# Revit family: 2019_ES_Ventana_Anicolor_Aji-HO-CE_2-Hojas_Oscilobatiente
name_source: partatom
category: Windows
units: mm (PartAtom-declared; Revit-internal decimal feet)

## family parameters
Always vertical = Yes
Cut with Voids When Loaded = No
Host = Wall
OmniClass Number = 23.30.20.00
OmniClass Title = Windows
Room Calculation Point = No
Shared = No

## types (2) — shared parameters
Abatible = No
Altura Máxima = 0.000 mm
Altura Mínima = 0.000 mm
Altura de antepecho por defecto = 500.000 mm
Altura mínima necessária = 0.000 mm
Analytic Construction = 1/4 in Pilkington single glazing
AnchoMarcoCentral = 101.000 mm
AnchoMarcoPerimetral = 69.300 mm
Anchura Máxima = 0.000 mm
Anchura Mínima = 0.000 mm
Aro = Aluminio
BIM Support = https://bimsupport.info
BIMEelementExpiryDate = 10/01/2021
BIMElementIssueDate = 10/01/2020
Bimetica = http://www.bimetica.com
BimeticaProductProfileURL = https://bimetica.com
ConfiguraçãoPoliamida = 273800 - 241200 - 961859
ControloDeFumos = No
CustoEnergéticoMj = 0 J
Define Thermal Properties by = Schematic Type
Description = Ventana 2 Hojas Practicables AJi HO CE de Anicolor
Enchimento = Vidro
Espaço livre acesso = 0.000 mm
EspesorPerfilesAluminio = 0.000 mm
EspessuraMaximaDoVidro = 0.000 mm
EspessuraMinimaDoVidro = 0.000 mm
Espuma = Espuma PIR entre varillas, galce del vidrio y marco
EstanquidadeÀÁgua = Clase E1650
GarantiaEstendida = Yes
GrosorHoja = 70.300 mm
Heat Transfer Coefficient (U) = 6.7018 W/(m²·K)
Historial = (RVT2019-V01) Creación de elemento.
HousingMaterial = <By Category>
IFCClassificação = IfcWindow
IfcExportAs = IfcWindow
IfcExportType = DoublePanelVertical
Intercalar = Technoform Warm Edge
IsExternal = Yes
LarguraPoliamidaAroFixo = 30.000 mm
LarguraPoliamidaFolha = 16.000 mm
Length = 0.000 mm
LicenseNumber = XXX-XXXX4564
Manija = Yes
Manufacturer = Anicolor
Marcado CE = Yes
MasterformatCode = 08 50 00
MasterformatTitle = Windows
Model = Aji HO CE
Motorizada = No
NúmeroSérie = AJi HO CE
OmniclassCode = 23-17 13 00
OmniclassTitle = Windows
Operation = Practicable. Ventana Practicable de dos hojas ocultas con apertura Interior
Oscilobatiente = No
PermeabilidadeAoAr = Clase 4
PesoBruto = 0.00 kg
PesoMáximoDaFolha = 0.00 kg
Poliamida = Technoform polyamide
PontoDeContato = Anicolor
Porcentaje materiales reciclados = 0.00%
Practicable = Yes
Prateleira interior = Yes
PrateleiraExterna = Yes
ProfundidadeDoAro = 73.600 mm
Referência = Aji HO CE
ResistênciaAoVento = Clase C5
SaídaEmergência = No
Series = AJi HO CE
Solar Heat Gain Coefficient = 0.86
TechnicalSupportContact = Anicolor
TelephoneContact = (+351) 234 729 420
Thermal Resistance (R) = 0.1492 (m²·K)/W
Total Y𝑔 = 0.044
Total 𝑈𝑔 = 0.6
UNSPSCCode = 30171600
UNSPSCTitle = Windows
URL = http://www.anicolor.pt
URL Poliamida = http://www.technoform.es
URL Poliamida - Catálogo = http://www.technoform.com
Uniclass2015Code = Ss_15_50_25
Uniclass2015Title = Doors, Windows And Glazing Survey Systems
Version = RVT2019
VersãoElementoBIM = V01
Vidro = <By Category>
Visual Light Transmittance = 0.9
Wall Closure = By host
Weight = 0.00 kg
Y𝑔 P1 = 0.044
Y𝑔 P2 = 0.044
ÉAcessível = Yes
ÉExterior = Yes
ÍndiceGlobalReduçãoAcústica = 43 (-2;-6)dB
𝑈𝑓 P1 = 2.591
𝑈𝑓 P2 = 3.087
𝑈𝑔 V1 = 0.6
𝑈𝑔 V2 = 0.6
zero-valued in all types: AcidificaçãoAtmosférica, AcidificaçãoAtmosféricaPorUnidade, CurvaSom, CustoEnergéticoKwh, CustoManutenção, DestruiçãoDaCamadaDeOzonoEstratosférica, DestruiçãoDaCamadaDeOzonoEstratosféricaPorUnidade, EmissãoCO2, Energia consumida, EnergiaNãoRenovávelConsumida, EnergiaNãoRenovávelConsumidaPorUnidade, EnergiaPrimáriaTotalConsumida, EnergiaPrimáriaTotalConsumidaPorUnidade, EnergiaRenovávelConsumida, EnergiaRenovávelConsumidaPorUnidade, Eutrofização, EutrofizaçãoPorUnidade, FaltaDeRecursos, FaltaDeRecursosPorUnidade, FatorSolarModificado, FatorSombra, FormaçãoFotoquímicaOzono, FormaçãoFotoquímicaOzonoPorUnidade, MassaSuperficialKgm2, MatériaPrima, MudançaClimática, MudançaClimáticaPorUnidade, ResiduoInerte, ResiduosNãoPerigosos, ResiduosNãoPerigososPorUnidade, ResiduosPerigososPorUnidade, ResíduoRadioativo, ResíduoRadioativoPorUnidade, ResíduosInertesPorUnidade, ResíduosPerigosos, ÁguaConsumida, ÁguaConsumidaPorUnidade

## per-type parameters (varying)
| type | Altura Real | Anchura Real | FraçãoDaÁreaDeVidro | GrosorAcristalamiento | GrosorAcristalamiento Real | Height | Height_2 | Perímetro | Total 𝐴𝑓 | Total 𝐴𝑔 | Total 𝑈𝑓 | Total 𝑙𝑔 | TransmitânciaTérmica | Width | Width_2 | Área | 𝐴𝑓 P1 | 𝐴𝑓 P2 | 𝐴𝑔 V1 | 𝐴𝑔 V2 | 𝑈𝑤 | 𝑙𝑔 P1 | 𝑙𝑔 P2 |
| 1310x2530 mm | 2460.000 mm | 1310.000 mm | 77.11% | 25.468 mm | 25.468 mm | 2460.000 mm | 2460.000 mm | 7540 | 0.737773 | 2.484827 | 2.748627 | 11.4264 | 1.2479 W/(m²·K) | 1310.000 mm | 1310.000 mm | 3.223 m² | 0.503 m² | 0.234 m² | 1.242 m² | 1.242 m² | 1.247912 | 6.7836 | 4.6428 |
| 1300x2530 mm | 2520.000 mm | 1300.000 mm | 77.08% | 30.000 mm | 30.000 mm | 2520.000 mm | 2520.000 mm | 7640 | 0.750763 | 2.525237 | 2.749903 | 11.6464 | 1.2491 W/(m²·K) | 1300.000 mm | 1300.000 mm | 3.276 m² | 0.510 m² | 0.241 m² | 1.263 m² | 1.263 m² | 1.249118 | 6.8836 | 4.7628 |

## geometry (parser evidence)
native form markers: Blend x2
no freeform markers — native parametric forms only
